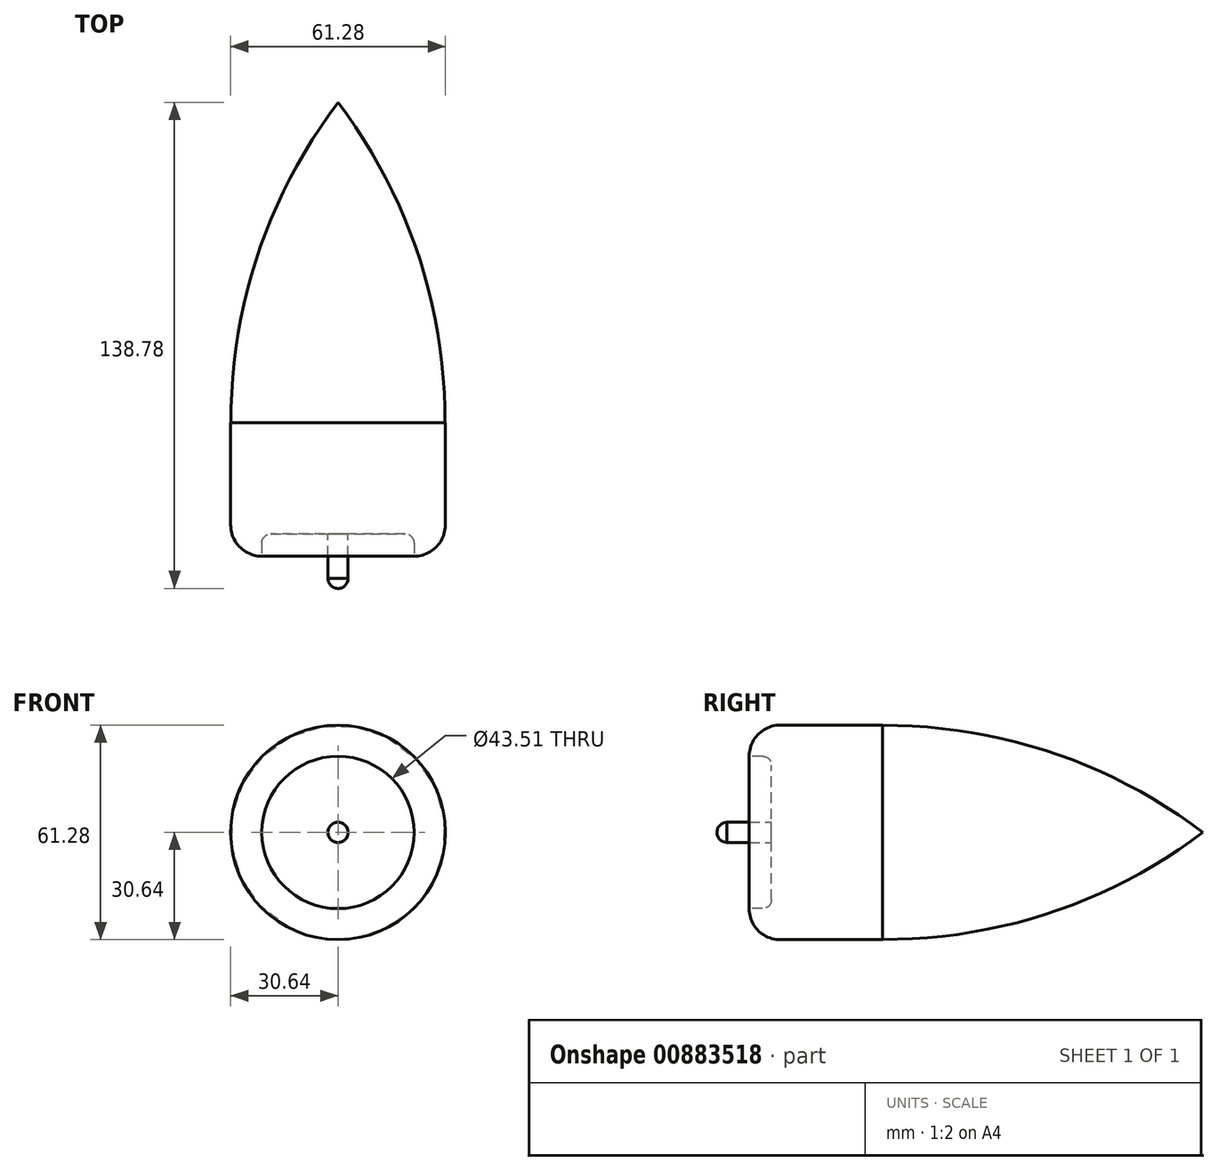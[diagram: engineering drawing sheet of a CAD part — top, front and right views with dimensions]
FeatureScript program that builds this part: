
annotation { "Feature Type Name" : "Feature", "Feature Type Description" : "" }
export const myFeature = defineFeature(function(context is Context, id is Id, definition is map)
    precondition{}
    {
        {
            var Q0;
            Q0=qCreatedBy(makeId("Front.planeOp"),FACE);
            var sketch = newSketch(context, id + "F0", { "sketchPlane" : qUnion([Q0])});
            skCircle(sketch, "E0", {"center": v(0, 0) * mm, "radius": 30.64 * mm});
            skSolve(sketch);
        }
        {
            var Q0;
            Q0 = qSketchRegion(id + "F0", true);
            extrude(context, id + "F1", {"entities" : qUnion([Q0]), "depth" : 38.1 * mm, "offsetDistance" : 25.4 * mm});
        }
        {
            var Q0;
            Q0=makeQuery(id+"F1.opExtrude","CAP_EDGE",EDGE,{"disambiguationData":[OSD([sQuery(id+"F0.wireOp",EDGE,"E0")])],"isStart":false});
            fillet(context, id + "F2", {"entities" : qUnion([Q0]), "radius" : 8.9 * mm, "tangentPropagation" : true, "allowEdgeOverflow" : false});
        }
        {
            var Q0;
            Q0=makeQuery(id+"F1.opExtrude","CAP_FACE",FACE,{"disambiguationData":[OSD([sQuery(id+"F0.wireOp",EDGE,"E0")])],"isStart":false});
            extrude(context, id + "F3", {"entities" : qUnion([Q0]), "operationType" : NewBodyOperationType.REMOVE, "oppositeDirection" : true, "depth" : 6.35 * mm, "offsetDistance" : 25.4 * mm});
        }
        {
            var Q0;
            Q0=makeQuery(id+"F3.boolean.opBoolean","COPY",FACE,{"derivedFrom":makeQuery(id+"F3.opExtrude","CAP_FACE",FACE,{"disambiguationData":[OSD([sQuery(id+"F0.wireOp",EDGE,"E0")])],"isStart":false})});
            var sketch = newSketch(context, id + "F4", { "sketchPlane" : qUnion([Q0])});
            skCircle(sketch, "E1", {"center": v(0, 0) * mm, "radius": 2.9 * mm});
            skSolve(sketch);
        }
        {
            var Q0;
            Q0 = qSketchRegion(id + "F4", true);
            extrude(context, id + "F5", {"entities" : qUnion([Q0]), "operationType" : NewBodyOperationType.ADD, "depth" : 12.7 * mm, "offsetDistance" : 25.4 * mm});
        }
        {
            var Q0;
            Q0=qCreatedBy(makeId("Right.planeOp"),FACE);
            var sketch = newSketch(context, id + "F6", { "sketchPlane" : qUnion([Q0])});
            skLineSegment(sketch, "E2", {"start": v(0, 0) * mm, "end": v(91.46, 0) * mm});
            skLineSegment(sketch, "E3", {"start": v(0, 0) * mm, "end": v(0, 30.57) * mm});
            skArc(sketch, "E4", {"start": v(91.46, 0) * mm, "mid": v(48.24, 22.81) * mm, "end": v(0, 30.57) * mm});
            skLineSegment(sketch, "E5", {"start": v(112.59, 0) * mm, "end": v(-18.46, 0) * mm, "construction": true});
            skLineSegment(sketch, "E6", {"start": v(91.46, 0) * mm, "end": v(0, 0) * mm});
            skSolve(sketch);
        }
        {
            var Q0;
            Q0 = qSketchRegion(id + "F6", true);
            var Q1;
            Q1=sQuery(id+"F6.wireOp",EDGE,"E5");
            revolve(context, id + "F7", {"operationType" : NewBodyOperationType.ADD, "surfaceOperationType" : NewSurfaceOperationType.NEW, "entities" : qUnion([Q0]), "axis" : qUnion([Q1]), "revolveType" : RevolveType.FULL});
        }
        {
            var Q0;
            Q0=makeQuery(id+"F5.opExtrude","CAP_FACE",FACE,{"disambiguationData":[OSD([sQuery(id+"F4.wireOp",EDGE,"E1")])],"isStart":false});
            var sketch = newSketch(context, id + "F8", { "sketchPlane" : qUnion([Q0])});
            skLineSegment(sketch, "E7", {"start": v(0, 2.9) * mm, "end": v(0, -2.9) * mm});
            skArc(sketch, "E8", {"start": v(0, -2.9) * mm, "mid": v(2.87, 0) * mm, "end": v(0, 2.9) * mm});
            skLineSegment(sketch, "E9", {"start": v(0, 3.8) * mm, "end": v(0, -3.62) * mm, "construction": true});
            skSolve(sketch);
        }
        {
            var Q0;
            Q0 = qSketchRegion(id + "F8", true);
            var Q1;
            Q1=sQuery(id+"F8.wireOp",EDGE,"E9");
            revolve(context, id + "F9", {"operationType" : NewBodyOperationType.ADD, "surfaceOperationType" : NewSurfaceOperationType.NEW, "entities" : qUnion([Q0]), "axis" : qUnion([Q1]), "revolveType" : RevolveType.FULL});
        }
        {
            var Q0;
            Q0=makeQuery(id+"F3.boolean.opBoolean","COPY",EDGE,{"derivedFrom":makeQuery(id+"F3.opExtrude","CAP_EDGE",EDGE,{"disambiguationData":[OSD([sQuery(id+"F0.wireOp",EDGE,"E0")])],"isStart":false})});
            fillet(context, id + "F10", {"entities" : qUnion([Q0]), "radius" : 2.54 * mm, "tangentPropagation" : true, "allowEdgeOverflow" : false});
        }
    });
